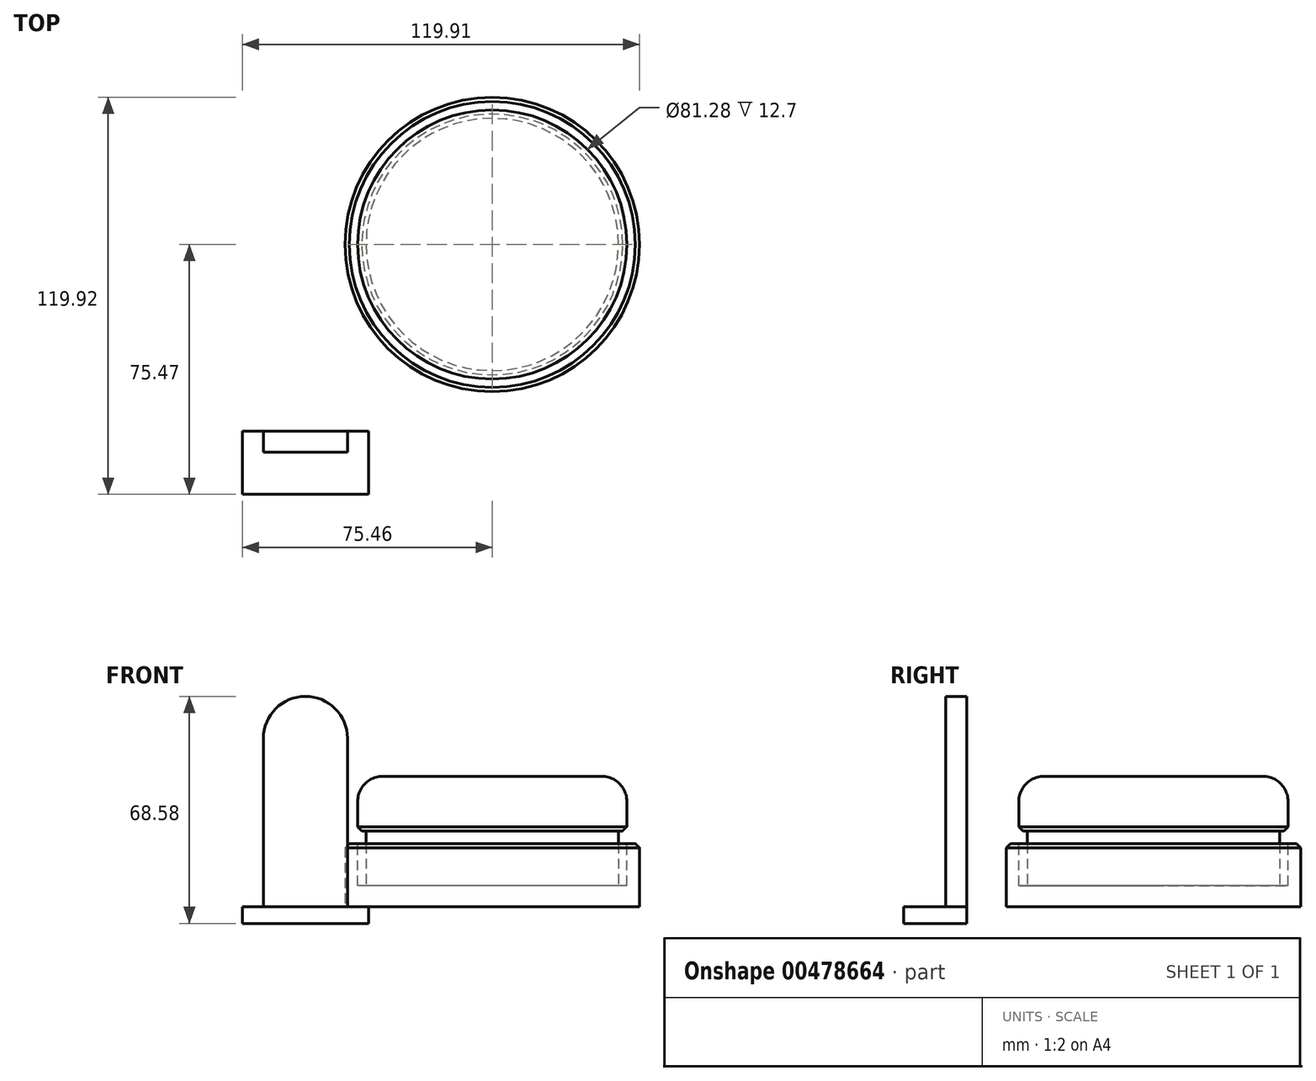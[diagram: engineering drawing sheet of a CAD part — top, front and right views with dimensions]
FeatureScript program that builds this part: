
annotation { "Feature Type Name" : "Feature", "Feature Type Description" : "" }
export const myFeature = defineFeature(function(context is Context, id is Id, definition is map)
    precondition{}
    {
        {
            var Q0;
            Q0=qCreatedBy(makeId("Top.planeOp"),FACE);
            var sketch = newSketch(context, id + "F0", { "sketchPlane" : qUnion([Q0])});
            skCircle(sketch, "E0", {"center": v(0, 0) * mm, "radius": 44.45 * mm});
            skSolve(sketch);
        }
        {
            var Q0;
            Q0=qSketchRegion(id+"F0",true);
            extrude(context, id + "F1", {"entities" : qUnion([Q0]), "depth" : 19.05 * mm});
        }
        {
            var Q0;
            Q0=makeQuery(id+"F1.opExtrude","CAP_FACE",FACE,{"disambiguationData":[OSD([sQuery(id+"F0.wireOp",EDGE,"E0")])],"isStart":false});
            var sketch = newSketch(context, id + "F2", { "sketchPlane" : qUnion([Q0])});
            skCircle(sketch, "E1", {"center": v(0, 0) * mm, "radius": 40.64 * mm});
            skSolve(sketch);
        }
        {
            var Q0;
            Q0=qSketchRegion(id+"F2",true);
            extrude(context, id + "F3", {"entities" : qUnion([Q0]), "operationType" : NewBodyOperationType.REMOVE, "oppositeDirection" : true, "depth" : 12.7 * mm});
        }
        {
            var Q0;
            Q0=makeQuery(id+"F3.boolean.opBoolean","COPY",FACE,{"derivedFrom":makeQuery(id+"F3.opExtrude","CAP_FACE",FACE,{"disambiguationData":[OSD([sQuery(id+"F2.wireOp",EDGE,"E1")])],"isStart":false})});
            var sketch = newSketch(context, id + "F4", { "sketchPlane" : qUnion([Q0])});
            skCircle(sketch, "E2", {"center": v(0, 0) * mm, "radius": 38.1 * mm});
            skSolve(sketch);
        }
        {
            var Q0;
            Q0=qSketchRegion(id+"F4",true);
            extrude(context, id + "F5", {"entities" : qUnion([Q0]), "depth" : 16.5 * mm});
        }
        {
            var Q0;
            Q0=makeQuery(id+"F5.opExtrude","CAP_FACE",FACE,{"disambiguationData":[OSD([sQuery(id+"F4.wireOp",EDGE,"E2")])],"isStart":false});
            var sketch = newSketch(context, id + "F6", { "sketchPlane" : qUnion([Q0])});
            skCircle(sketch, "E3", {"center": v(0, 0) * mm, "radius": 40.64 * mm});
            skSolve(sketch);
        }
        {
            var Q0;
            Q0=qSketchRegion(id+"F6",true);
            extrude(context, id + "F7", {"entities" : qUnion([Q0]), "operationType" : NewBodyOperationType.ADD, "depth" : 16.5 * mm});
        }
        {
            var Q0;
            Q0=makeQuery(id+"F7.opExtrude","CAP_EDGE",EDGE,{"disambiguationData":[OSD([sQuery(id+"F6.wireOp",EDGE,"E3")])],"isStart":false});
            fillet(context, id + "F8", {"entities" : qUnion([Q0]), "radius" : 7.62 * mm, "tangentPropagation" : true, "allowEdgeOverflow" : false});
        }
        {
            var Q0;
            Q0=makeQuery(id+"F1.opExtrude","CAP_EDGE",EDGE,{"disambiguationData":[OSD([sQuery(id+"F0.wireOp",EDGE,"E0")])],"isStart":false});
            var Q1;
            Q1=makeQuery(id+"F7.opExtrude","CAP_EDGE",EDGE,{"disambiguationData":[OSD([sQuery(id+"F6.wireOp",EDGE,"E3")])],"isStart":true});
            chamfer(context, id + "F9", {"entities" : qUnion([Q0, Q1]), "width" : 1.27 * mm, "tangentPropagation" : true});
        }
        {
            var Q0;
            Q0=qCreatedBy(makeId("Top.planeOp"),FACE);
            var sketch = newSketch(context, id + "F10", { "sketchPlane" : qUnion([Q0])});
            skLineSegment(sketch, "E4.bottom", {"start": v(-75.46, -56.42) * mm, "end": v(-37.36, -56.42) * mm});
            skLineSegment(sketch, "E4.top", {"start": v(-75.46, -75.47) * mm, "end": v(-37.36, -75.47) * mm});
            skLineSegment(sketch, "E4.left", {"start": v(-75.46, -56.42) * mm, "end": v(-75.46, -75.47) * mm});
            skLineSegment(sketch, "E4.right", {"start": v(-37.36, -56.42) * mm, "end": v(-37.36, -75.47) * mm});
            skSolve(sketch);
        }
        {
            var Q0;
            Q0=qSketchRegion(id+"F10",true);
            extrude(context, id + "F11", {"entities" : qUnion([Q0]), "oppositeDirection" : true, "depth" : 5.08 * mm});
        }
        {
            var Q0;
            Q0=makeQuery(id+"F11.opExtrude","CAP_FACE",FACE,{"disambiguationData":[OSD([sQuery(id+"F10.wireOp",EDGE,"E4.bottom"),sQuery(id+"F10.wireOp",EDGE,"E4.top"),sQuery(id+"F10.wireOp",EDGE,"E4.left"),sQuery(id+"F10.wireOp",EDGE,"E4.right")])],"isStart":true});
            var sketch = newSketch(context, id + "F12", { "sketchPlane" : qUnion([Q0])});
            skLineSegment(sketch, "E5.bottom", {"start": v(-69.11, -56.42) * mm, "end": v(-43.71, -56.42) * mm});
            skLineSegment(sketch, "E5.top", {"start": v(-69.11, -62.77) * mm, "end": v(-43.71, -62.77) * mm});
            skLineSegment(sketch, "E5.left", {"start": v(-69.11, -56.42) * mm, "end": v(-69.11, -62.77) * mm});
            skLineSegment(sketch, "E5.right", {"start": v(-43.71, -56.42) * mm, "end": v(-43.71, -62.77) * mm});
            skSolve(sketch);
        }
        {
            var Q0;
            Q0=qSketchRegion(id+"F12",true);
            extrude(context, id + "F13", {"entities" : qUnion([Q0]), "operationType" : NewBodyOperationType.ADD, "depth" : 50.8 * mm});
        }
        {
            var Q0;
            Q0=makeQuery(id+"F13.opExtrude","SWEPT_FACE",FACE,{"disambiguationData":[OSD([sQuery(id+"F12.wireOp",EDGE,"E5.top")])]});
            var sketch = newSketch(context, id + "F14", { "sketchPlane" : qUnion([Q0])});
            skArc(sketch, "E6", {"start": v(-43.71, 50.8) * mm, "mid": v(-56.41, 63.5) * mm, "end": v(-69.11, 50.8) * mm});
            skLineSegment(sketch, "E7", {"start": v(-69.11, 50.8) * mm, "end": v(-43.71, 50.8) * mm});
            skSolve(sketch);
        }
        {
            var Q0;
            Q0=qSketchRegion(id+"F14",true);
            extrude(context, id + "F15", {"entities" : qUnion([Q0]), "operationType" : NewBodyOperationType.ADD, "oppositeDirection" : true, "depth" : 6.35 * mm});
        }
    });
